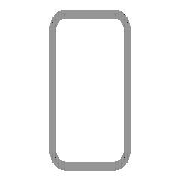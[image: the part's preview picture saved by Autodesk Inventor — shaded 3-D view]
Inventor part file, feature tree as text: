
AUTODESK INVENTOR PART (.ipt)
format: ipt  version: 2025 (Build 290162010, 162A)  size: 146,432 bytes
history: native  units: mm (DEFAULTED — no unit token found)
features: other x4, sketch x1, plane x1
ambient origin geometry x8: Origin, YZ Plane, XZ Plane, XY Plane, X Axis, Y Axis, Z Axis, Center Point
bodies: Solid1 (feature_tree), Body (feature_tree)
feature tree (6):
  parser-record x1  (decoder bookkeeping rows leaked as tree rows — omitted from the tree; the rows remain in map.json)
  other  "Driven Length"
  other  "Start Plane"
  other  "End Plane"
  sketch  "Sketch3"  dims[d3=3000.0mm d4=0.0mm d7=4.5mm d10=60.0mm d11=40.0mm d12=3.0mm d13=-0.0mm d14=3000.0mm d15=30.0mm d16=20.0mm d17=90.0deg d18=3000.0mm]
  plane  "Work Plane3"
